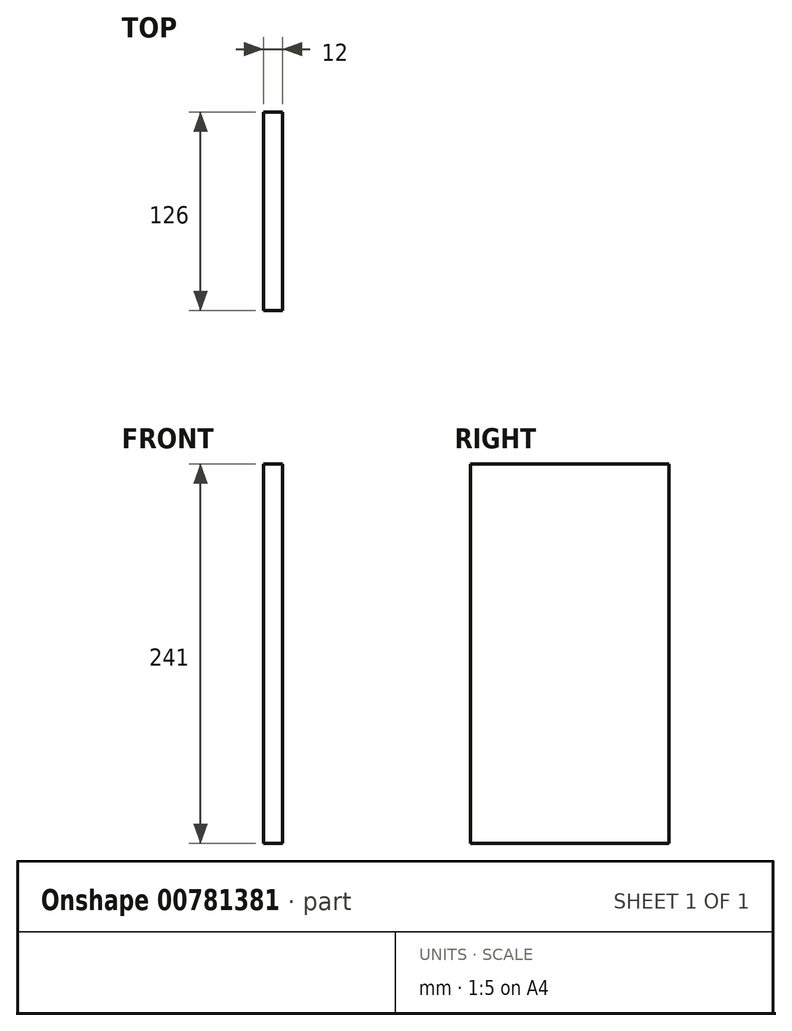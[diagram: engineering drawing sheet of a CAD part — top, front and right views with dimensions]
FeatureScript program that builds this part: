
annotation { "Feature Type Name" : "Feature", "Feature Type Description" : "" }
export const myFeature = defineFeature(function(context is Context, id is Id, definition is map)
    precondition{}
    {
        {
            var Q0;
            Q0=qCreatedBy(makeId("Right.planeOp"),FACE);
            var sketch = newSketch(context, id + "F0", { "sketchPlane" : qUnion([Q0])});
            skLineSegment(sketch, "E0.bottom", {"start": v(-63, -120.5) * mm, "end": v(63, -120.5) * mm});
            skLineSegment(sketch, "E0.top", {"start": v(-63, 120.5) * mm, "end": v(63, 120.5) * mm});
            skLineSegment(sketch, "E0.left", {"start": v(-63, -120.5) * mm, "end": v(-63, 120.5) * mm});
            skLineSegment(sketch, "E0.right", {"start": v(63, -120.5) * mm, "end": v(63, 120.5) * mm});
            skPoint(sketch, "E0.middle", {"position": v(0, 0) * mm});
            skSolve(sketch);
        }
        {
            var Q0;
            Q0=makeQuery(id+"F0.imprint","IMPRINT",FACE,{"disambiguationData":[TD([[makeQuery(id+"F0.imprint","IMPRINT",EDGE,{"derivedFrom":sQuery(id+"F0.wireOp",EDGE,"E0.bottom")}),1.0]])]});
            extrude(context, id + "F1", {"entities" : qUnion([Q0]), "depth" : 12 * mm, "offsetDistance" : 25 * mm});
        }
    });
